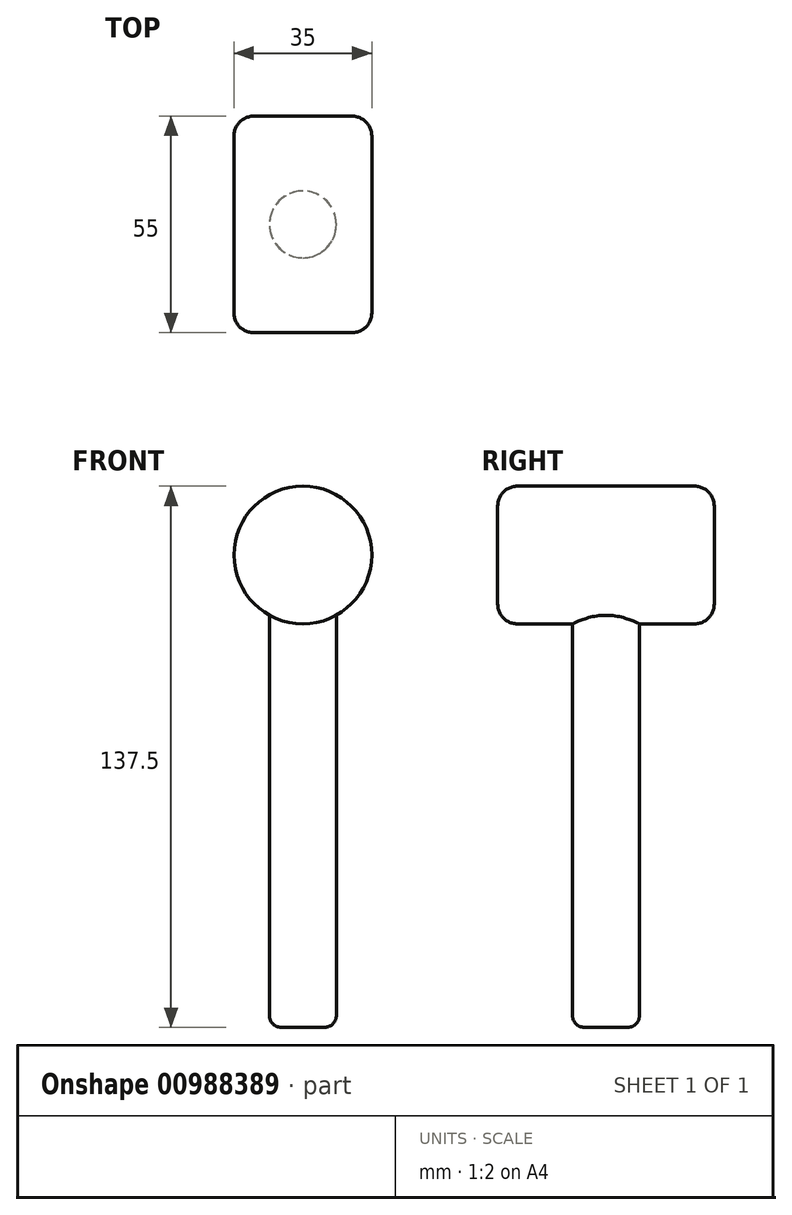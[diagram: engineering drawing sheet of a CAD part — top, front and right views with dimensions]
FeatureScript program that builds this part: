
annotation { "Feature Type Name" : "Feature", "Feature Type Description" : "" }
export const myFeature = defineFeature(function(context is Context, id is Id, definition is map)
    precondition{}
    {
        {
            var Q0;
            Q0=qCreatedBy(makeId("Front.planeOp"),FACE);
            var sketch = newSketch(context, id + "F0", { "sketchPlane" : qUnion([Q0])});
            skCircle(sketch, "E0", {"center": v(0, 0) * mm, "radius": 17.5 * mm});
            skSolve(sketch);
        }
        {
            var Q0;
            Q0 = qSketchRegion(id + "F0", true);
            extrude(context, id + "F1", {"entities" : qUnion([Q0]), "endBound" : BoundingType.SYMMETRIC, "depth" : 55 * mm, "offsetDistance" : 25 * mm});
        }
        {
            var Q0;
            Q0=qCreatedBy(makeId("Top.planeOp"),FACE);
            var sketch = newSketch(context, id + "F2", { "sketchPlane" : qUnion([Q0])});
            skCircle(sketch, "E1", {"center": v(0, 0) * mm, "radius": 8.5 * mm});
            skSolve(sketch);
        }
        {
            var Q0;
            Q0 = qSketchRegion(id + "F2", true);
            extrude(context, id + "F3", {"entities" : qUnion([Q0]), "operationType" : NewBodyOperationType.ADD, "oppositeDirection" : true, "depth" : 120 * mm, "offsetDistance" : 25 * mm});
        }
        {
            var Q0;
            Q0=makeQuery(id+"F1.opExtrude","CAP_EDGE",EDGE,{"disambiguationData":[OSD([sQuery(id+"F0.wireOp",EDGE,"E0")])],"isStart":true});
            var Q1;
            Q1=makeQuery(id+"F1.opExtrude","CAP_EDGE",EDGE,{"disambiguationData":[OSD([sQuery(id+"F0.wireOp",EDGE,"E0")])],"isStart":false});
            fillet(context, id + "F4", {"entities" : qUnion([Q0, Q1]), "radius" : 5 * mm, "tangentPropagation" : true, "allowEdgeOverflow" : false});
        }
        {
            var Q0;
            Q0=makeQuery(id+"F3.opExtrude","CAP_EDGE",EDGE,{"disambiguationData":[OSD([sQuery(id+"F2.wireOp",EDGE,"E1")])],"isStart":false});
            fillet(context, id + "F5", {"entities" : qUnion([Q0]), "radius" : 3 * mm, "tangentPropagation" : true, "allowEdgeOverflow" : false});
        }
    });
